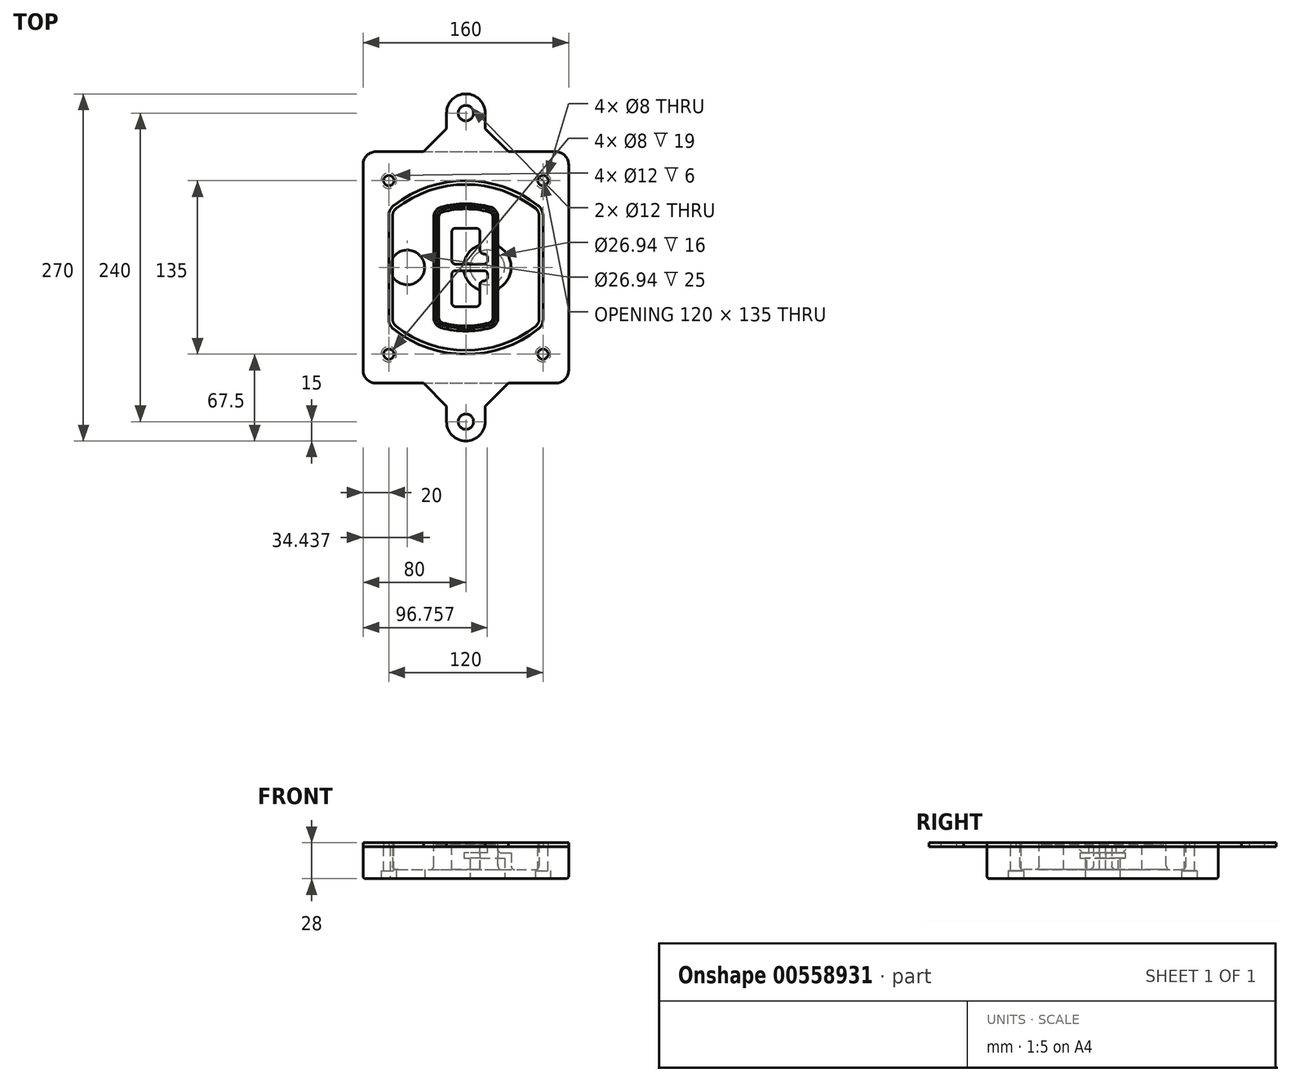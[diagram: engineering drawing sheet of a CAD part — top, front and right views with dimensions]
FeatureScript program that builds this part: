
annotation { "Feature Type Name" : "Feature", "Feature Type Description" : "" }
export const myFeature = defineFeature(function(context is Context, id is Id, definition is map)
    precondition{}
    {
        {
            var Q0;
            Q0=qCreatedBy(makeId("Top.planeOp"),FACE);
            var sketch = newSketch(context, id + "F0", { "sketchPlane" : qUnion([Q0])});
            skPoint(sketch, "E0.rect.middle", {"position": v(0, 0) * mm});
            skLineSegment(sketch, "E1.bottom", {"start": v(-70, -90) * mm, "end": v(70, -90) * mm});
            skLineSegment(sketch, "E1.top", {"start": v(-70, 90) * mm, "end": v(70, 90) * mm});
            skLineSegment(sketch, "E1.left", {"start": v(-80, -80) * mm, "end": v(-80, 80) * mm});
            skLineSegment(sketch, "E1.right", {"start": v(80, -80) * mm, "end": v(80, 80) * mm});
            skLineSegment(sketch, "E2", {"start": v(-80, 90) * mm, "end": v(80, -90) * mm, "construction": true});
            skLineSegment(sketch, "E3", {"start": v(80, 90) * mm, "end": v(-80, -90) * mm, "construction": true});
            skCircle(sketch, "E4", {"center": v(-60, 67.5) * mm, "radius": 4 * mm});
            skCircle(sketch, "E5", {"center": v(60, 67.5) * mm, "radius": 4 * mm});
            skCircle(sketch, "E6", {"center": v(60, -67.5) * mm, "radius": 4 * mm});
            skCircle(sketch, "E7", {"center": v(-60, -67.5) * mm, "radius": 4 * mm});
            skLineSegment(sketch, "E8", {"start": v(-60, 67.5) * mm, "end": v(60, 67.5) * mm, "construction": true});
            skLineSegment(sketch, "E9", {"start": v(60, 67.5) * mm, "end": v(60, -67.5) * mm, "construction": true});
            skLineSegment(sketch, "E10", {"start": v(60, -67.5) * mm, "end": v(-60, -67.5) * mm, "construction": true});
            skLineSegment(sketch, "E11", {"start": v(-60, -67.5) * mm, "end": v(-60, 67.5) * mm, "construction": true});
            skLineSegment(sketch, "E12", {"start": v(-60, 40.3) * mm, "end": v(-60, -40.3) * mm});
            skLineSegment(sketch, "E13", {"start": v(60, 40.3) * mm, "end": v(60, -40.3) * mm});
            skArc(sketch, "E14", {"start": v(56.15, 48.18) * mm, "mid": v(0, 67.5) * mm, "end": v(-56.15, 48.18) * mm});
            skArc(sketch, "E15", {"start": v(-56.15, -48.18) * mm, "mid": v(0, -67.5) * mm, "end": v(56.15, -48.18) * mm});
            skLineSegment(sketch, "E16", {"start": v(-60, 0) * mm, "end": v(60, 0) * mm, "construction": true});
            skPoint(sketch, "E17.visualSharp", {"position": v(-60, -45) * mm});
            skArc(sketch, "E17.filletArc", {"start": v(-60, -40.3) * mm, "mid": v(-58.99, -44.68) * mm, "end": v(-56.15, -48.18) * mm});
            skPoint(sketch, "E18.visualSharp", {"position": v(-60, 45) * mm});
            skArc(sketch, "E18.filletArc", {"start": v(-56.15, 48.18) * mm, "mid": v(-58.99, 44.68) * mm, "end": v(-60, 40.3) * mm});
            skPoint(sketch, "E19.visualSharp", {"position": v(60, 45) * mm});
            skArc(sketch, "E19.filletArc", {"start": v(60, 40.3) * mm, "mid": v(58.99, 44.68) * mm, "end": v(56.15, 48.18) * mm});
            skPoint(sketch, "E20.visualSharp", {"position": v(60, -45) * mm});
            skArc(sketch, "E20.filletArc", {"start": v(56.15, -48.18) * mm, "mid": v(58.99, -44.68) * mm, "end": v(60, -40.3) * mm});
            skPoint(sketch, "E21.visualSharp", {"position": v(-80, 90) * mm});
            skArc(sketch, "E21.filletArc", {"start": v(-70, 90) * mm, "mid": v(-77.07, 87.07) * mm, "end": v(-80, 80) * mm});
            skPoint(sketch, "E22.visualSharp", {"position": v(80, 90) * mm});
            skArc(sketch, "E22.filletArc", {"start": v(80, 80) * mm, "mid": v(77.07, 87.07) * mm, "end": v(70, 90) * mm});
            skPoint(sketch, "E23.visualSharp", {"position": v(80, -90) * mm});
            skArc(sketch, "E23.filletArc", {"start": v(70, -90) * mm, "mid": v(77.07, -87.07) * mm, "end": v(80, -80) * mm});
            skPoint(sketch, "E24.visualSharp", {"position": v(-80, -90) * mm});
            skArc(sketch, "E24.filletArc", {"start": v(-80, -80) * mm, "mid": v(-77.07, -87.07) * mm, "end": v(-70, -90) * mm});
            skArc(sketch, "E25.0", {"start": v(57, 40.3) * mm, "mid": v(56.3, 43.36) * mm, "end": v(54.3, 45.81) * mm});
            skLineSegment(sketch, "E25.1", {"start": v(57, 40.3) * mm, "end": v(57, -40.3) * mm});
            skArc(sketch, "E25.2", {"start": v(54.3, -45.81) * mm, "mid": v(56.3, -43.36) * mm, "end": v(57, -40.3) * mm});
            skArc(sketch, "E25.3", {"start": v(-54.3, -45.81) * mm, "mid": v(0, -64.5) * mm, "end": v(54.3, -45.81) * mm});
            skArc(sketch, "E25.4", {"start": v(-57, -40.3) * mm, "mid": v(-56.3, -43.36) * mm, "end": v(-54.3, -45.81) * mm});
            skArc(sketch, "E25.5", {"start": v(54.3, 45.81) * mm, "mid": v(0, 64.5) * mm, "end": v(-54.3, 45.81) * mm});
            skLineSegment(sketch, "E25.6", {"start": v(-57, 40.3) * mm, "end": v(-57, -40.3) * mm});
            skArc(sketch, "E25.7", {"start": v(-54.3, 45.81) * mm, "mid": v(-56.3, 43.36) * mm, "end": v(-57, 40.3) * mm});
            skArc(sketch, "E26.0", {"start": v(-58.62, 51.33) * mm, "mid": v(-62.58, 46.43) * mm, "end": v(-64, 40.3) * mm});
            skArc(sketch, "E26.1", {"start": v(58.62, 51.33) * mm, "mid": v(0, 71.5) * mm, "end": v(-58.62, 51.33) * mm});
            skArc(sketch, "E26.2", {"start": v(64, 40.3) * mm, "mid": v(62.58, 46.43) * mm, "end": v(58.62, 51.33) * mm});
            skLineSegment(sketch, "E26.3", {"start": v(64, 40.3) * mm, "end": v(64, -40.3) * mm});
            skArc(sketch, "E26.4", {"start": v(58.62, -51.33) * mm, "mid": v(62.58, -46.43) * mm, "end": v(64, -40.3) * mm});
            skLineSegment(sketch, "E26.5", {"start": v(-64, 40.3) * mm, "end": v(-64, -40.3) * mm});
            skArc(sketch, "E26.6", {"start": v(-58.62, -51.33) * mm, "mid": v(0, -71.5) * mm, "end": v(58.62, -51.33) * mm});
            skArc(sketch, "E26.7", {"start": v(-64, -40.3) * mm, "mid": v(-62.58, -46.43) * mm, "end": v(-58.62, -51.33) * mm});
            skSolve(sketch);
        }
        {
            var Q0;
            Q0=makeQuery(id+"F0.imprint","IMPRINT",FACE,{"disambiguationData":[TD([[makeQuery(id+"F0.imprint","IMPRINT",EDGE,{"derivedFrom":sQuery(id+"F0.wireOp",EDGE,"E1.bottom")}),1.0]])]});
            var Q1;
            Q1=makeQuery(id+"F0.imprint","IMPRINT",FACE,{"disambiguationData":[TD([[makeQuery(id+"F0.imprint","IMPRINT",EDGE,{"derivedFrom":sQuery(id+"F0.wireOp",EDGE,"E12")}),1.0]])]});
            var Q2;
            Q2=makeQuery(id+"F0.imprint","IMPRINT",FACE,{"disambiguationData":[TD([[makeQuery(id+"F0.imprint","IMPRINT",EDGE,{"derivedFrom":sQuery(id+"F0.wireOp",EDGE,"E25.0")}),1.0]])]});
            var Q3;
            Q3=makeQuery(id+"F0.imprint","IMPRINT",FACE,{"disambiguationData":[TD([[makeQuery(id+"F0.imprint","IMPRINT",EDGE,{"derivedFrom":sQuery(id+"F0.wireOp",EDGE,"E12")}),-1.0]])]});
            extrude(context, id + "F1", {"entities" : qUnion([Q0, Q1, Q2, Q3]), "oppositeDirection" : true, "depth" : 25 * mm});
        }
        {
            var Q0;
            Q0=makeQuery(id+"F0.imprint","IMPRINT",FACE,{"disambiguationData":[TD([[makeQuery(id+"F0.imprint","IMPRINT",EDGE,{"derivedFrom":sQuery(id+"F0.wireOp",EDGE,"E12")}),1.0]])]});
            extrude(context, id + "F2", {"entities" : qUnion([Q0]), "operationType" : NewBodyOperationType.ADD, "depth" : 3 * mm});
        }
        {
            var Q0;
            Q0=makeQuery(id+"F0.imprint","IMPRINT",FACE,{"disambiguationData":[TD([[makeQuery(id+"F0.imprint","IMPRINT",EDGE,{"derivedFrom":sQuery(id+"F0.wireOp",EDGE,"E25.0")}),1.0]])]});
            extrude(context, id + "F3", {"entities" : qUnion([Q0]), "operationType" : NewBodyOperationType.REMOVE, "oppositeDirection" : true, "depth" : 18 * mm});
        }
        {
            var Q0;
            Q0=makeQuery(id+"F2.opExtrude","CAP_FACE",FACE,{"disambiguationData":[OSD([sQuery(id+"F0.wireOp",EDGE,"E12"),sQuery(id+"F0.wireOp",EDGE,"E13"),sQuery(id+"F0.wireOp",EDGE,"E14"),sQuery(id+"F0.wireOp",EDGE,"E15"),sQuery(id+"F0.wireOp",EDGE,"E17.filletArc"),sQuery(id+"F0.wireOp",EDGE,"E18.filletArc"),sQuery(id+"F0.wireOp",EDGE,"E19.filletArc"),sQuery(id+"F0.wireOp",EDGE,"E20.filletArc"),sQuery(id+"F0.wireOp",EDGE,"E25.0"),sQuery(id+"F0.wireOp",EDGE,"E25.1"),sQuery(id+"F0.wireOp",EDGE,"E25.2"),sQuery(id+"F0.wireOp",EDGE,"E25.3"),sQuery(id+"F0.wireOp",EDGE,"E25.4"),sQuery(id+"F0.wireOp",EDGE,"E25.5"),sQuery(id+"F0.wireOp",EDGE,"E25.6"),sQuery(id+"F0.wireOp",EDGE,"E25.7")])],"isStart":false});
            var sketch = newSketch(context, id + "F4", { "sketchPlane" : qUnion([Q0])});
            skArc(sketch, "E27.0", {"start": v(-19.08, -46.97) * mm, "mid": v(0, -49.5) * mm, "end": v(19.08, -46.97) * mm});
            skArc(sketch, "E28.0", {"start": v(19.08, 46.97) * mm, "mid": v(0, 49.5) * mm, "end": v(-19.08, 46.97) * mm});
            skLineSegment(sketch, "E29", {"start": v(-25, 39.25) * mm, "end": v(-25, -39.25) * mm});
            skLineSegment(sketch, "E30", {"start": v(25, 39.25) * mm, "end": v(25, -39.25) * mm});
            skLineSegment(sketch, "E31", {"start": v(-25, 45.1) * mm, "end": v(25, 45.1) * mm, "construction": true});
            skLineSegment(sketch, "E32", {"start": v(-25, -45.1) * mm, "end": v(25, -45.1) * mm, "construction": true});
            skPoint(sketch, "E33.visualSharp", {"position": v(-25, 45.1) * mm});
            skArc(sketch, "E33.filletArc", {"start": v(-19.08, 46.97) * mm, "mid": v(-23.35, 44.11) * mm, "end": v(-25, 39.25) * mm});
            skPoint(sketch, "E34.visualSharp", {"position": v(25, 45.1) * mm});
            skArc(sketch, "E34.filletArc", {"start": v(25, 39.25) * mm, "mid": v(23.35, 44.11) * mm, "end": v(19.08, 46.97) * mm});
            skPoint(sketch, "E35.visualSharp", {"position": v(25, -45.1) * mm});
            skArc(sketch, "E35.filletArc", {"start": v(19.08, -46.97) * mm, "mid": v(23.35, -44.11) * mm, "end": v(25, -39.25) * mm});
            skPoint(sketch, "E36.visualSharp", {"position": v(-25, -45.1) * mm});
            skArc(sketch, "E36.filletArc", {"start": v(-25, -39.25) * mm, "mid": v(-23.35, -44.11) * mm, "end": v(-19.08, -46.97) * mm});
            skArc(sketch, "E37.0", {"start": v(54.3, 45.81) * mm, "mid": v(0, 64.5) * mm, "end": v(-54.3, 45.81) * mm});
            skArc(sketch, "E37.1", {"start": v(-54.3, 45.81) * mm, "mid": v(-56.3, 43.36) * mm, "end": v(-57, 40.3) * mm});
            skLineSegment(sketch, "E37.2", {"start": v(-57, 40.3) * mm, "end": v(-57, -40.3) * mm});
            skArc(sketch, "E37.3", {"start": v(-57, -40.3) * mm, "mid": v(-56.3, -43.36) * mm, "end": v(-54.3, -45.81) * mm});
            skArc(sketch, "E37.4", {"start": v(-54.3, -45.81) * mm, "mid": v(0, -64.5) * mm, "end": v(54.3, -45.81) * mm});
            skArc(sketch, "E37.5", {"start": v(54.3, -45.81) * mm, "mid": v(56.3, -43.36) * mm, "end": v(57, -40.3) * mm});
            skLineSegment(sketch, "E37.6", {"start": v(57, 40.3) * mm, "end": v(57, -40.3) * mm});
            skArc(sketch, "E37.7", {"start": v(57, 40.3) * mm, "mid": v(56.3, 43.36) * mm, "end": v(54.3, 45.81) * mm});
            skLineSegment(sketch, "E38.0", {"start": v(23, 39.25) * mm, "end": v(23, -39.25) * mm});
            skArc(sketch, "E38.1", {"start": v(18.56, -45.04) * mm, "mid": v(21.76, -42.9) * mm, "end": v(23, -39.25) * mm});
            skArc(sketch, "E38.2", {"start": v(-18.56, -45.04) * mm, "mid": v(0, -47.5) * mm, "end": v(18.56, -45.04) * mm});
            skArc(sketch, "E38.3", {"start": v(-23, -39.25) * mm, "mid": v(-21.76, -42.9) * mm, "end": v(-18.56, -45.04) * mm});
            skLineSegment(sketch, "E38.4", {"start": v(-23, 39.25) * mm, "end": v(-23, -39.25) * mm});
            skArc(sketch, "E38.5", {"start": v(23, 39.25) * mm, "mid": v(21.76, 42.9) * mm, "end": v(18.56, 45.04) * mm});
            skArc(sketch, "E38.6", {"start": v(-18.56, 45.04) * mm, "mid": v(-21.76, 42.9) * mm, "end": v(-23, 39.25) * mm});
            skArc(sketch, "E38.7", {"start": v(18.56, 45.04) * mm, "mid": v(0, 47.5) * mm, "end": v(-18.56, 45.04) * mm});
            skArc(sketch, "E39.0", {"start": v(21, 39.25) * mm, "mid": v(20.18, 41.68) * mm, "end": v(18.04, 43.1) * mm});
            skLineSegment(sketch, "E39.1", {"start": v(21, 39.25) * mm, "end": v(21, -39.25) * mm});
            skArc(sketch, "E39.2", {"start": v(18.04, -43.1) * mm, "mid": v(20.18, -41.68) * mm, "end": v(21, -39.25) * mm});
            skArc(sketch, "E39.3", {"start": v(-18.04, -43.1) * mm, "mid": v(0, -45.5) * mm, "end": v(18.04, -43.1) * mm});
            skArc(sketch, "E39.4", {"start": v(-21, -39.25) * mm, "mid": v(-20.18, -41.68) * mm, "end": v(-18.04, -43.1) * mm});
            skArc(sketch, "E39.5", {"start": v(18.04, 43.1) * mm, "mid": v(0, 45.5) * mm, "end": v(-18.04, 43.1) * mm});
            skLineSegment(sketch, "E39.6", {"start": v(-21, 39.25) * mm, "end": v(-21, -39.25) * mm});
            skArc(sketch, "E39.7", {"start": v(-18.04, 43.1) * mm, "mid": v(-20.18, 41.68) * mm, "end": v(-21, 39.25) * mm});
            skLineSegment(sketch, "E40", {"start": v(-25, 0) * mm, "end": v(25, 0) * mm, "construction": true});
            skLineSegment(sketch, "E41", {"start": v(-11, 5.5) * mm, "end": v(-11, 27.5) * mm});
            skLineSegment(sketch, "E42", {"start": v(-8, 30.5) * mm, "end": v(8, 30.5) * mm});
            skLineSegment(sketch, "E43", {"start": v(11, 27.5) * mm, "end": v(11, 13.5) * mm});
            skLineSegment(sketch, "E44", {"start": v(14, 10.5) * mm, "end": v(14, 10.5) * mm});
            skLineSegment(sketch, "E45", {"start": v(17, 7.5) * mm, "end": v(17, 5.5) * mm});
            skLineSegment(sketch, "E46", {"start": v(14, 2.5) * mm, "end": v(-8, 2.5) * mm});
            skPoint(sketch, "E47.visualSharp", {"position": v(-11, 30.5) * mm});
            skArc(sketch, "E47.filletArc", {"start": v(-8, 30.5) * mm, "mid": v(-10.12, 29.62) * mm, "end": v(-11, 27.5) * mm});
            skPoint(sketch, "E48.visualSharp", {"position": v(11, 30.5) * mm});
            skArc(sketch, "E48.filletArc", {"start": v(11, 27.5) * mm, "mid": v(10.12, 29.62) * mm, "end": v(8, 30.5) * mm});
            skPoint(sketch, "E49.visualSharp", {"position": v(11, 10.5) * mm});
            skArc(sketch, "E49.filletArc", {"start": v(11, 13.5) * mm, "mid": v(11.88, 11.38) * mm, "end": v(14, 10.5) * mm});
            skPoint(sketch, "E50.visualSharp", {"position": v(17, 10.5) * mm});
            skArc(sketch, "E50.filletArc", {"start": v(17, 7.5) * mm, "mid": v(16.12, 9.62) * mm, "end": v(14, 10.5) * mm});
            skPoint(sketch, "E51.visualSharp", {"position": v(17, 2.5) * mm});
            skArc(sketch, "E51.filletArc", {"start": v(14, 2.5) * mm, "mid": v(16.12, 3.38) * mm, "end": v(17, 5.5) * mm});
            skPoint(sketch, "E52.visualSharp", {"position": v(-11, 2.5) * mm});
            skArc(sketch, "E52.filletArc", {"start": v(-11, 5.5) * mm, "mid": v(-10.12, 3.38) * mm, "end": v(-8, 2.5) * mm});
            skLineSegment(sketch, "E53.0.MirrorCS", {"start": v(14, -2.5) * mm, "end": v(-8, -2.5) * mm});
            skArc(sketch, "E54.0.MirrorCS", {"start": v(-11, -5.5) * mm, "mid": v(-10.12, -3.38) * mm, "end": v(-8, -2.5) * mm});
            skLineSegment(sketch, "E55.0.MirrorCS", {"start": v(-11, -5.5) * mm, "end": v(-11, -27.5) * mm});
            skArc(sketch, "E56.0.MirrorCS", {"start": v(-8, -30.5) * mm, "mid": v(-10.12, -29.62) * mm, "end": v(-11, -27.5) * mm});
            skLineSegment(sketch, "E57.0.MirrorCS", {"start": v(-8, -30.5) * mm, "end": v(8, -30.5) * mm});
            skArc(sketch, "E58.0.MirrorCS", {"start": v(11, -27.5) * mm, "mid": v(10.12, -29.62) * mm, "end": v(8, -30.5) * mm});
            skLineSegment(sketch, "E59.0.MirrorCS", {"start": v(11, -27.5) * mm, "end": v(11, -13.5) * mm});
            skArc(sketch, "E60.0.MirrorCS", {"start": v(11, -13.5) * mm, "mid": v(11.88, -11.38) * mm, "end": v(14, -10.5) * mm});
            skArc(sketch, "E61.0.MirrorCS", {"start": v(17, -7.5) * mm, "mid": v(16.12, -9.62) * mm, "end": v(14, -10.5) * mm});
            skLineSegment(sketch, "E62.0.MirrorCS", {"start": v(17, -7.5) * mm, "end": v(17, -5.5) * mm});
            skArc(sketch, "E63.0.MirrorCS", {"start": v(14, -2.5) * mm, "mid": v(16.12, -3.38) * mm, "end": v(17, -5.5) * mm});
            skSolve(sketch);
        }
        {
            var Q0;
            Q0=makeQuery(id+"F4.imprint","IMPRINT",FACE,{"disambiguationData":[TD([[makeQuery(id+"F4.imprint","IMPRINT",EDGE,{"derivedFrom":sQuery(id+"F4.wireOp",EDGE,"E27.0")}),1.0]])]});
            var Q1;
            Q1=makeQuery(id+"F4.imprint","IMPRINT",FACE,{"disambiguationData":[TD([[makeQuery(id+"F4.imprint","IMPRINT",EDGE,{"derivedFrom":sQuery(id+"F4.wireOp",EDGE,"E38.0")}),-1.0]])]});
            var Q2;
            Q2=makeQuery(id+"F4.imprint","IMPRINT",FACE,{"disambiguationData":[TD([[makeQuery(id+"F4.imprint","IMPRINT",EDGE,{"derivedFrom":sQuery(id+"F4.wireOp",EDGE,"E39.0")}),1.0]])]});
            extrude(context, id + "F5", {"entities" : qUnion([Q0, Q1, Q2]), "operationType" : NewBodyOperationType.ADD, "endBound" : BoundingType.UP_TO_NEXT, "oppositeDirection" : true, "depth" : 25 * mm});
        }
        {
            var Q0;
            Q0=makeQuery(id+"F4.imprint","IMPRINT",FACE,{"disambiguationData":[TD([[makeQuery(id+"F4.imprint","IMPRINT",EDGE,{"derivedFrom":sQuery(id+"F4.wireOp",EDGE,"E38.0")}),-1.0]])]});
            extrude(context, id + "F6", {"entities" : qUnion([Q0]), "operationType" : NewBodyOperationType.REMOVE, "oppositeDirection" : true, "depth" : 2 * mm});
        }
        {
            var Q0;
            Q0=makeQuery(id+"F1.opExtrude","CAP_FACE",FACE,{"disambiguationData":[OSD([sQuery(id+"F0.wireOp",EDGE,"E1.bottom"),sQuery(id+"F0.wireOp",EDGE,"E1.top"),sQuery(id+"F0.wireOp",EDGE,"E1.left"),sQuery(id+"F0.wireOp",EDGE,"E1.right"),sQuery(id+"F0.wireOp",EDGE,"E4"),sQuery(id+"F0.wireOp",EDGE,"E5"),sQuery(id+"F0.wireOp",EDGE,"E6"),sQuery(id+"F0.wireOp",EDGE,"E7"),sQuery(id+"F0.wireOp",EDGE,"E21.filletArc"),sQuery(id+"F0.wireOp",EDGE,"E22.filletArc"),sQuery(id+"F0.wireOp",EDGE,"E23.filletArc"),sQuery(id+"F0.wireOp",EDGE,"E24.filletArc")])],"isStart":false});
            var sketch = newSketch(context, id + "F7", { "sketchPlane" : qUnion([Q0])});
            skCircle(sketch, "E64", {"center": v(16.76, 0) * mm, "radius": 13.47 * mm});
            skCircle(sketch, "E65", {"center": v(-45.56, 0) * mm, "radius": 13.47 * mm});
            skLineSegment(sketch, "E66", {"start": v(80, 0) * mm, "end": v(-80, 0) * mm});
            skCircle(sketch, "E67", {"center": v(16.76, 0) * mm, "radius": 18.47 * mm});
            skCircle(sketch, "E68", {"center": v(60, -67.5) * mm, "radius": 6 * mm});
            skCircle(sketch, "E69", {"center": v(-60, -67.5) * mm, "radius": 6 * mm});
            skCircle(sketch, "E70", {"center": v(-60, 67.5) * mm, "radius": 6 * mm});
            skCircle(sketch, "E71", {"center": v(60, 67.5) * mm, "radius": 6 * mm});
            skSolve(sketch);
        }
        {
            var Q0;
            {var subQ1=sQuery(id+"F7.wireOp",EDGE,"E66");var subQ4=sQuery(id+"F7.wireOp",EDGE,"E64");var subQ6=makeQuery(id+"F7.imprint","INTERSECT",VERTEX,{"disambiguationData":[OD(0.0)],"derivedFrom":[subQ4,subQ1]});Q0=makeQuery(id+"F7.imprint","IMPRINT",FACE,{"disambiguationData":[TD([[makeQuery(id+"F7.imprint","IMPRINT",EDGE,{"disambiguationData":[TD([[subQ6,-1.0]])],"derivedFrom":subQ4}),-1.0]])]});}
            var Q1;
            {var subQ0=sQuery(id+"F7.wireOp",EDGE,"E66");var subQ1=sQuery(id+"F7.wireOp",EDGE,"E64");var subQ3=makeQuery(id+"F7.imprint","INTERSECT",VERTEX,{"disambiguationData":[OD(0.0)],"derivedFrom":[subQ1,subQ0]});Q1=makeQuery(id+"F7.imprint","IMPRINT",FACE,{"disambiguationData":[TD([[makeQuery(id+"F7.imprint","IMPRINT",EDGE,{"disambiguationData":[TD([[subQ3,-1.0]])],"derivedFrom":subQ1}),1.0]])]});}
            var Q2;
            {var subQ0=sQuery(id+"F7.wireOp",EDGE,"E66");var subQ1=sQuery(id+"F7.wireOp",EDGE,"E64");var subQ3=makeQuery(id+"F7.imprint","INTERSECT",VERTEX,{"disambiguationData":[OD(0.0)],"derivedFrom":[subQ1,subQ0]});Q2=makeQuery(id+"F7.imprint","IMPRINT",FACE,{"disambiguationData":[TD([[makeQuery(id+"F7.imprint","IMPRINT",EDGE,{"disambiguationData":[TD([[subQ3,1.0]])],"derivedFrom":subQ1}),1.0]])]});}
            var Q3;
            {var subQ1=sQuery(id+"F7.wireOp",EDGE,"E66");var subQ4=sQuery(id+"F7.wireOp",EDGE,"E64");var subQ6=makeQuery(id+"F7.imprint","INTERSECT",VERTEX,{"disambiguationData":[OD(0.0)],"derivedFrom":[subQ4,subQ1]});Q3=makeQuery(id+"F7.imprint","IMPRINT",FACE,{"disambiguationData":[TD([[makeQuery(id+"F7.imprint","IMPRINT",EDGE,{"disambiguationData":[TD([[subQ6,1.0]])],"derivedFrom":subQ4}),-1.0]])]});}
            extrude(context, id + "F8", {"entities" : qUnion([Q0, Q1, Q2, Q3]), "operationType" : NewBodyOperationType.ADD, "oppositeDirection" : true, "depth" : 20 * mm});
        }
        {
            var Q0;
            {var subQ0=sQuery(id+"F7.wireOp",EDGE,"E66");var subQ1=sQuery(id+"F7.wireOp",EDGE,"E64");var subQ3=makeQuery(id+"F7.imprint","INTERSECT",VERTEX,{"disambiguationData":[OD(0.0)],"derivedFrom":[subQ1,subQ0]});Q0=makeQuery(id+"F7.imprint","IMPRINT",FACE,{"disambiguationData":[TD([[makeQuery(id+"F7.imprint","IMPRINT",EDGE,{"disambiguationData":[TD([[subQ3,-1.0]])],"derivedFrom":subQ1}),1.0]])]});}
            var Q1;
            {var subQ0=sQuery(id+"F7.wireOp",EDGE,"E66");var subQ1=sQuery(id+"F7.wireOp",EDGE,"E64");var subQ3=makeQuery(id+"F7.imprint","INTERSECT",VERTEX,{"disambiguationData":[OD(0.0)],"derivedFrom":[subQ1,subQ0]});Q1=makeQuery(id+"F7.imprint","IMPRINT",FACE,{"disambiguationData":[TD([[makeQuery(id+"F7.imprint","IMPRINT",EDGE,{"disambiguationData":[TD([[subQ3,1.0]])],"derivedFrom":subQ1}),1.0]])]});}
            extrude(context, id + "F9", {"entities" : qUnion([Q0, Q1]), "operationType" : NewBodyOperationType.REMOVE, "oppositeDirection" : true, "depth" : 16 * mm});
        }
        {
            var Q0;
            {var subQ0=sQuery(id+"F7.wireOp",EDGE,"E66");var subQ1=sQuery(id+"F7.wireOp",EDGE,"E65");var subQ3=makeQuery(id+"F7.imprint","INTERSECT",VERTEX,{"disambiguationData":[OD(0.0)],"derivedFrom":[subQ1,subQ0]});Q0=makeQuery(id+"F7.imprint","IMPRINT",FACE,{"disambiguationData":[TD([[makeQuery(id+"F7.imprint","IMPRINT",EDGE,{"disambiguationData":[TD([[subQ3,-1.0]])],"derivedFrom":subQ1}),1.0]])]});}
            var Q1;
            {var subQ0=sQuery(id+"F7.wireOp",EDGE,"E66");var subQ1=sQuery(id+"F7.wireOp",EDGE,"E65");var subQ3=makeQuery(id+"F7.imprint","INTERSECT",VERTEX,{"disambiguationData":[OD(0.0)],"derivedFrom":[subQ1,subQ0]});Q1=makeQuery(id+"F7.imprint","IMPRINT",FACE,{"disambiguationData":[TD([[makeQuery(id+"F7.imprint","IMPRINT",EDGE,{"disambiguationData":[TD([[subQ3,1.0]])],"derivedFrom":subQ1}),1.0]])]});}
            extrude(context, id + "F10", {"entities" : qUnion([Q0, Q1]), "operationType" : NewBodyOperationType.REMOVE, "oppositeDirection" : true, "depth" : 25 * mm});
        }
        {
            var Q0;
            Q0=makeQuery(id+"F7.imprint","IMPRINT",FACE,{"disambiguationData":[TD([[makeQuery(id+"F7.imprint","IMPRINT",EDGE,{"derivedFrom":sQuery(id+"F7.wireOp",EDGE,"E68")}),1.0]])]});
            var Q1;
            Q1=makeQuery(id+"F7.imprint","IMPRINT",FACE,{"disambiguationData":[TD([[makeQuery(id+"F7.imprint","IMPRINT",EDGE,{"derivedFrom":makeQuery(id+"F1.opExtrude","CAP_EDGE",EDGE,{"disambiguationData":[OSD([sQuery(id+"F0.wireOp",EDGE,"E5")])],"isStart":false})}),-1.0]])]});
            var Q2;
            Q2=makeQuery(id+"F7.imprint","IMPRINT",FACE,{"disambiguationData":[TD([[makeQuery(id+"F7.imprint","IMPRINT",EDGE,{"derivedFrom":sQuery(id+"F7.wireOp",EDGE,"E69")}),1.0]])]});
            var Q3;
            Q3=makeQuery(id+"F7.imprint","IMPRINT",FACE,{"disambiguationData":[TD([[makeQuery(id+"F7.imprint","IMPRINT",EDGE,{"derivedFrom":makeQuery(id+"F1.opExtrude","CAP_EDGE",EDGE,{"disambiguationData":[OSD([sQuery(id+"F0.wireOp",EDGE,"E4")])],"isStart":false})}),-1.0]])]});
            var Q4;
            Q4=makeQuery(id+"F7.imprint","IMPRINT",FACE,{"disambiguationData":[TD([[makeQuery(id+"F7.imprint","IMPRINT",EDGE,{"derivedFrom":sQuery(id+"F7.wireOp",EDGE,"E70")}),1.0]])]});
            var Q5;
            Q5=makeQuery(id+"F7.imprint","IMPRINT",FACE,{"disambiguationData":[TD([[makeQuery(id+"F7.imprint","IMPRINT",EDGE,{"derivedFrom":makeQuery(id+"F1.opExtrude","CAP_EDGE",EDGE,{"disambiguationData":[OSD([sQuery(id+"F0.wireOp",EDGE,"E7")])],"isStart":false})}),-1.0]])]});
            var Q6;
            Q6=makeQuery(id+"F7.imprint","IMPRINT",FACE,{"disambiguationData":[TD([[makeQuery(id+"F7.imprint","IMPRINT",EDGE,{"derivedFrom":sQuery(id+"F7.wireOp",EDGE,"E71")}),1.0]])]});
            var Q7;
            Q7=makeQuery(id+"F7.imprint","IMPRINT",FACE,{"disambiguationData":[TD([[makeQuery(id+"F7.imprint","IMPRINT",EDGE,{"derivedFrom":makeQuery(id+"F1.opExtrude","CAP_EDGE",EDGE,{"disambiguationData":[OSD([sQuery(id+"F0.wireOp",EDGE,"E6")])],"isStart":false})}),-1.0]])]});
            extrude(context, id + "F11", {"entities" : qUnion([Q0, Q1, Q2, Q3, Q4, Q5, Q6, Q7]), "operationType" : NewBodyOperationType.REMOVE, "oppositeDirection" : true, "depth" : 6 * mm});
        }
        {
            var Q0;
            Q0=makeQuery(id+"F9.boolean.opBoolean","COPY",FACE,{"derivedFrom":makeQuery(id+"F9.opExtrude","CAP_FACE",FACE,{"disambiguationData":[OSD([sQuery(id+"F7.wireOp",EDGE,"E64")])],"isStart":false})});
            var sketch = newSketch(context, id + "F12", { "sketchPlane" : qUnion([Q0])});
            skArc(sketch, "E72.0", {"start": v(11, 17.55) * mm, "mid": v(2.57, 11.82) * mm, "end": v(-1.54, 2.5) * mm});
            skArc(sketch, "E72.1", {"start": v(-1.54, -2.5) * mm, "mid": v(2.57, -11.82) * mm, "end": v(11, -17.55) * mm});
            skLineSegment(sketch, "E73", {"start": v(-1.54, -2.5) * mm, "end": v(14, -2.5) * mm});
            skLineSegment(sketch, "E74.0", {"start": v(14, 2.5) * mm, "end": v(-1.54, 2.5) * mm});
            skArc(sketch, "E74.1", {"start": v(14, 2.5) * mm, "mid": v(16.12, 3.38) * mm, "end": v(17, 5.5) * mm});
            skLineSegment(sketch, "E74.2", {"start": v(17, 7.5) * mm, "end": v(17, 5.5) * mm});
            skArc(sketch, "E74.3", {"start": v(17, 7.5) * mm, "mid": v(16.12, 9.62) * mm, "end": v(14, 10.5) * mm});
            skArc(sketch, "E74.4", {"start": v(11, 13.5) * mm, "mid": v(11.88, 11.38) * mm, "end": v(14, 10.5) * mm});
            skLineSegment(sketch, "E74.5", {"start": v(11, 17.55) * mm, "end": v(11, 13.5) * mm});
            skLineSegment(sketch, "E74.7", {"start": v(14, -2.5) * mm, "end": v(-1.54, -2.5) * mm});
            skArc(sketch, "E74.8", {"start": v(14, -2.5) * mm, "mid": v(16.12, -3.38) * mm, "end": v(17, -5.5) * mm});
            skLineSegment(sketch, "E74.9", {"start": v(17, -7.5) * mm, "end": v(17, -5.5) * mm});
            skArc(sketch, "E74.10", {"start": v(17, -7.5) * mm, "mid": v(16.12, -9.62) * mm, "end": v(14, -10.5) * mm});
            skArc(sketch, "E74.11", {"start": v(11, -13.5) * mm, "mid": v(11.88, -11.38) * mm, "end": v(14, -10.5) * mm});
            skLineSegment(sketch, "E74.12", {"start": v(11, -17.55) * mm, "end": v(11, -13.5) * mm});
            skPoint(sketch, "E75.orphan", {"position": v(11, -27.5) * mm});
            skPoint(sketch, "E76.orphan", {"position": v(-8, -2.5) * mm});
            skPoint(sketch, "E77.orphan", {"position": v(-8, 2.5) * mm});
            skPoint(sketch, "E78.orphan", {"position": v(11, 27.5) * mm});
            skSolve(sketch);
        }
        {
            var Q0;
            {var subQ7=sQuery(id+"F12.wireOp",EDGE,"E72.0");var subQ14=sQuery(id+"F12.wireOp",EDGE,"E72.1");var subQ16=sQuery(id+"F12.wireOp",EDGE,"E74.1");var subQ18=sQuery(id+"F12.wireOp",EDGE,"E74.8");Q0=qUnion([makeQuery(id+"F12.imprint","IMPRINT",FACE,{"disambiguationData":[TD([[makeQuery(id+"F12.imprint","IMPRINT",EDGE,{"derivedFrom":subQ7}),1.0]])]}),makeQuery(id+"F12.imprint","IMPRINT",FACE,{"disambiguationData":[TD([[makeQuery(id+"F12.imprint","IMPRINT",EDGE,{"derivedFrom":subQ14}),1.0]])]}),makeQuery(id+"F12.imprint","IMPRINT",FACE,{"disambiguationData":[TD([[makeQuery(id+"F12.imprint","IMPRINT",EDGE,{"derivedFrom":subQ16}),1.0]])]}),makeQuery(id+"F12.imprint","IMPRINT",FACE,{"disambiguationData":[TD([[makeQuery(id+"F12.imprint","IMPRINT",EDGE,{"derivedFrom":subQ18}),-1.0]])]})]);}
            var Q1;
            Q1=makeQuery(id+"F5.boolean.opBoolean","SPLIT",FACE,{"disambiguationData":[TD([makeQuery(id+"F5.opExtrude","SWEPT_FACE",FACE,{"disambiguationData":[OSD([sQuery(id+"F4.wireOp",EDGE,"E41")])]})])],"derivedFrom":makeQuery(id+"F3.boolean.opBoolean","COPY",FACE,{"derivedFrom":makeQuery(id+"F3.opExtrude","CAP_FACE",FACE,{"disambiguationData":[OSD([sQuery(id+"F0.wireOp",EDGE,"E25.0"),sQuery(id+"F0.wireOp",EDGE,"E25.1"),sQuery(id+"F0.wireOp",EDGE,"E25.2"),sQuery(id+"F0.wireOp",EDGE,"E25.3"),sQuery(id+"F0.wireOp",EDGE,"E25.4"),sQuery(id+"F0.wireOp",EDGE,"E25.5"),sQuery(id+"F0.wireOp",EDGE,"E25.6"),sQuery(id+"F0.wireOp",EDGE,"E25.7")])],"isStart":false})})});
            extrude(context, id + "F13", {"entities" : qUnion([Q0]), "operationType" : NewBodyOperationType.REMOVE, "endBound" : BoundingType.UP_TO_SURFACE, "endBoundEntityFace" : qUnion([Q1]), "depth" : 25 * mm});
        }
        {
            var Q0;
            Q0=makeQuery(id+"F3.boolean.opBoolean","COPY",EDGE,{"derivedFrom":makeQuery(id+"F3.opExtrude","CAP_EDGE",EDGE,{"disambiguationData":[OSD([sQuery(id+"F0.wireOp",EDGE,"E25.6")])],"isStart":false})});
            var Q1;
            Q1=makeQuery(id+"F8.boolean.opBoolean","INTERSECT",EDGE,{"derivedFrom":[makeQuery(id+"F5.opExtrude","SWEPT_FACE",FACE,{"disambiguationData":[OSD([sQuery(id+"F4.wireOp",EDGE,"E30")])]}),makeQuery(id+"F8.opExtrude","CAP_FACE",FACE,{"disambiguationData":[OSD([sQuery(id+"F7.wireOp",EDGE,"E67")])],"isStart":false})]});
            var Q2;
            Q2=makeQuery(id+"F8.boolean.opBoolean","INTERSECT",EDGE,{"disambiguationData":[OD(1.0)],"derivedFrom":[makeQuery(id+"F5.opExtrude","SWEPT_FACE",FACE,{"disambiguationData":[OSD([sQuery(id+"F4.wireOp",EDGE,"E30")])]}),makeQuery(id+"F8.opExtrude","SWEPT_FACE",FACE,{"disambiguationData":[OSD([sQuery(id+"F7.wireOp",EDGE,"E67")])]})]});
            var Q3;
            {var subQ0=sQuery(id+"F4.wireOp",EDGE,"E30");Q3=makeQuery(id+"F8.boolean.opBoolean","SPLIT",EDGE,{"disambiguationData":[TD([makeQuery(id+"F5.opExtrude","SWEPT_FACE",FACE,{"disambiguationData":[OSD([sQuery(id+"F4.wireOp",EDGE,"E35.filletArc")])]})])],"derivedFrom":makeQuery(id+"F5.opExtrude","CAP_EDGE",EDGE,{"disambiguationData":[OSD([subQ0])],"isStart":false})});}
            var Q4;
            {var subQ0=sQuery(id+"F0.wireOp",EDGE,"E25.7");var subQ1=sQuery(id+"F0.wireOp",EDGE,"E25.1");var subQ2=sQuery(id+"F0.wireOp",EDGE,"E25.6");var subQ3=sQuery(id+"F0.wireOp",EDGE,"E25.5");var subQ4=sQuery(id+"F0.wireOp",EDGE,"E25.4");var subQ5=sQuery(id+"F0.wireOp",EDGE,"E25.0");var subQ6=sQuery(id+"F0.wireOp",EDGE,"E25.2");var subQ7=sQuery(id+"F0.wireOp",EDGE,"E25.3");Q4=makeQuery(id+"F8.boolean.opBoolean","INTERSECT",EDGE,{"derivedFrom":[makeQuery(id+"F5.boolean.opBoolean","SPLIT",FACE,{"disambiguationData":[TD([makeQuery(id+"F2.opExtrude","SWEPT_FACE",FACE,{"disambiguationData":[OSD([subQ5])]})])],"derivedFrom":makeQuery(id+"F3.boolean.opBoolean","COPY",FACE,{"derivedFrom":makeQuery(id+"F3.opExtrude","CAP_FACE",FACE,{"disambiguationData":[OSD([subQ5,subQ1,subQ6,subQ7,subQ4,subQ3,subQ2,subQ0])],"isStart":false})})}),makeQuery(id+"F8.opExtrude","SWEPT_FACE",FACE,{"disambiguationData":[OSD([sQuery(id+"F7.wireOp",EDGE,"E67")])]})]});}
            var Q5;
            Q5=makeQuery(id+"F8.boolean.opBoolean","INTERSECT",EDGE,{"disambiguationData":[OD(0.0)],"derivedFrom":[makeQuery(id+"F5.opExtrude","SWEPT_FACE",FACE,{"disambiguationData":[OSD([sQuery(id+"F4.wireOp",EDGE,"E30")])]}),makeQuery(id+"F8.opExtrude","SWEPT_FACE",FACE,{"disambiguationData":[OSD([sQuery(id+"F7.wireOp",EDGE,"E67")])]})]});
            fillet(context, id + "F14", {"entities" : qUnion([Q0, Q1, Q2, Q3, Q4, Q5]), "radius" : 3 * mm, "tangentPropagation" : true, "allowEdgeOverflow" : false});
        }
        {
            var Q0;
            Q0=makeQuery(id+"F1.opExtrude","CAP_EDGE",EDGE,{"disambiguationData":[OSD([sQuery(id+"F0.wireOp",EDGE,"E1.bottom")])],"isStart":false});
            fillet(context, id + "F15", {"entities" : qUnion([Q0]), "radius" : 2 * mm, "tangentPropagation" : true, "allowEdgeOverflow" : false});
        }
        {
            var Q0;
            {var subQ0=sQuery(id+"F0.wireOp",EDGE,"E21.filletArc");var subQ1=sQuery(id+"F0.wireOp",EDGE,"E7");var subQ2=sQuery(id+"F0.wireOp",EDGE,"E6");var subQ3=sQuery(id+"F0.wireOp",EDGE,"E5");var subQ4=sQuery(id+"F0.wireOp",EDGE,"E4");var subQ5=sQuery(id+"F0.wireOp",EDGE,"E22.filletArc");var subQ6=sQuery(id+"F0.wireOp",EDGE,"E1.bottom");var subQ7=sQuery(id+"F0.wireOp",EDGE,"E1.right");var subQ8=sQuery(id+"F0.wireOp",EDGE,"E1.top");var subQ9=sQuery(id+"F0.wireOp",EDGE,"E1.left");var subQ10=sQuery(id+"F0.wireOp",EDGE,"E23.filletArc");var subQ11=sQuery(id+"F0.wireOp",EDGE,"E24.filletArc");Q0=makeQuery(id+"F2.boolean.opBoolean","SPLIT",FACE,{"disambiguationData":[TD([makeQuery(id+"F1.opExtrude","SWEPT_FACE",FACE,{"disambiguationData":[OSD([subQ6])]})])],"derivedFrom":makeQuery(id+"F1.opExtrude","CAP_FACE",FACE,{"disambiguationData":[OSD([subQ6,subQ8,subQ9,subQ7,subQ4,subQ3,subQ2,subQ1,subQ0,subQ5,subQ10,subQ11])],"isStart":true})});}
            var sketch = newSketch(context, id + "F16", { "sketchPlane" : qUnion([Q0])});
            skArc(sketch, "E79.0", {"start": v(56.15, 48.18) * mm, "mid": v(0, 67.5) * mm, "end": v(-56.15, 48.18) * mm});
            skLineSegment(sketch, "E79.1", {"start": v(-60, 40.3) * mm, "end": v(-60, -40.3) * mm});
            skArc(sketch, "E79.2", {"start": v(-56.15, -48.18) * mm, "mid": v(0, -67.5) * mm, "end": v(56.15, -48.18) * mm});
            skLineSegment(sketch, "E79.3", {"start": v(60, 40.3) * mm, "end": v(60, -40.3) * mm});
            skLineSegment(sketch, "E79.4", {"start": v(-70, 90) * mm, "end": v(70, 90) * mm});
            skArc(sketch, "E79.5", {"start": v(80, 80) * mm, "mid": v(77.07, 87.07) * mm, "end": v(70, 90) * mm});
            skLineSegment(sketch, "E79.6", {"start": v(80, -80) * mm, "end": v(80, 80) * mm});
            skArc(sketch, "E79.7", {"start": v(70, -90) * mm, "mid": v(77.07, -87.07) * mm, "end": v(80, -80) * mm});
            skLineSegment(sketch, "E79.8", {"start": v(-70, -90) * mm, "end": v(70, -90) * mm});
            skArc(sketch, "E79.9", {"start": v(-80, -80) * mm, "mid": v(-77.07, -87.07) * mm, "end": v(-70, -90) * mm});
            skLineSegment(sketch, "E79.10", {"start": v(-80, -80) * mm, "end": v(-80, 80) * mm});
            skArc(sketch, "E79.11", {"start": v(-70, 90) * mm, "mid": v(-77.07, 87.07) * mm, "end": v(-80, 80) * mm});
            skArc(sketch, "E79.12", {"start": v(-56.15, 48.18) * mm, "mid": v(-58.99, 44.68) * mm, "end": v(-60, 40.3) * mm});
            skArc(sketch, "E79.13", {"start": v(-60, -40.3) * mm, "mid": v(-58.99, -44.68) * mm, "end": v(-56.15, -48.18) * mm});
            skArc(sketch, "E79.14", {"start": v(56.15, -48.18) * mm, "mid": v(58.99, -44.68) * mm, "end": v(60, -40.3) * mm});
            skArc(sketch, "E79.15", {"start": v(60, 40.3) * mm, "mid": v(58.99, 44.68) * mm, "end": v(56.15, 48.18) * mm});
            skLineSegment(sketch, "E80", {"start": v(0, 50.03) * mm, "end": v(0, 142.28) * mm, "construction": true});
            skLineSegment(sketch, "E81", {"start": v(-33, 90) * mm, "end": v(-15, 108) * mm});
            skLineSegment(sketch, "E82", {"start": v(-15, 108) * mm, "end": v(-15, 120) * mm});
            skLineSegment(sketch, "E83", {"start": v(33, 90) * mm, "end": v(15, 108) * mm});
            skLineSegment(sketch, "E84", {"start": v(15, 108) * mm, "end": v(15, 120) * mm});
            skArc(sketch, "E85", {"start": v(15, 120) * mm, "mid": v(0, 135) * mm, "end": v(-15, 120) * mm});
            skCircle(sketch, "E86", {"center": v(0, 120) * mm, "radius": 6 * mm});
            skLineSegment(sketch, "E87", {"start": v(94.87, 0) * mm, "end": v(-91.8, 0) * mm, "construction": true});
            skPoint(sketch, "E87.startSnap0", {"position": v(80, 0) * mm});
            skPoint(sketch, "E87.endSnap0", {"position": v(-80, 0) * mm});
            skLineSegment(sketch, "E88.MirrorCS", {"start": v(-33, -90) * mm, "end": v(-15, -108) * mm});
            skLineSegment(sketch, "E89.MirrorCS", {"start": v(-15, -108) * mm, "end": v(-15, -120) * mm});
            skArc(sketch, "E90.MirrorCS", {"start": v(15, -120) * mm, "mid": v(0, -135) * mm, "end": v(-15, -120) * mm});
            skCircle(sketch, "E91.MirrorC", {"center": v(0, -120) * mm, "radius": 6 * mm});
            skLineSegment(sketch, "E92.MirrorCS", {"start": v(15, -108) * mm, "end": v(15, -120) * mm});
            skLineSegment(sketch, "E93.MirrorCS", {"start": v(33, -90) * mm, "end": v(15, -108) * mm});
            skSolve(sketch);
        }
        {
            var Q0;
            {var subQ1=sQuery(id+"F16.wireOp",EDGE,"E81");Q0=makeQuery(id+"F16.imprint","IMPRINT",FACE,{"disambiguationData":[TD([[makeQuery(id+"F16.imprint","IMPRINT",EDGE,{"derivedFrom":subQ1}),-1.0]])]});}
            var Q1;
            {var subQ0=sQuery(id+"F16.wireOp",EDGE,"E88.MirrorCS");Q1=makeQuery(id+"F16.imprint","IMPRINT",FACE,{"disambiguationData":[TD([[makeQuery(id+"F16.imprint","IMPRINT",EDGE,{"derivedFrom":subQ0}),1.0]])]});}
            var Q2;
            Q2=makeQuery(id+"F16.imprint","IMPRINT",FACE,{"disambiguationData":[TD([[makeQuery(id+"F16.imprint","IMPRINT",EDGE,{"derivedFrom":sQuery(id+"F16.wireOp",EDGE,"E79.0")}),-1.0]])]});
            var Q3;
            Q3=makeQuery(id+"F2.opExtrude","CAP_FACE",FACE,{"disambiguationData":[OSD([sQuery(id+"F0.wireOp",EDGE,"E12"),sQuery(id+"F0.wireOp",EDGE,"E13"),sQuery(id+"F0.wireOp",EDGE,"E14"),sQuery(id+"F0.wireOp",EDGE,"E15"),sQuery(id+"F0.wireOp",EDGE,"E17.filletArc"),sQuery(id+"F0.wireOp",EDGE,"E18.filletArc"),sQuery(id+"F0.wireOp",EDGE,"E19.filletArc"),sQuery(id+"F0.wireOp",EDGE,"E20.filletArc"),sQuery(id+"F0.wireOp",EDGE,"E25.0"),sQuery(id+"F0.wireOp",EDGE,"E25.1"),sQuery(id+"F0.wireOp",EDGE,"E25.2"),sQuery(id+"F0.wireOp",EDGE,"E25.3"),sQuery(id+"F0.wireOp",EDGE,"E25.4"),sQuery(id+"F0.wireOp",EDGE,"E25.5"),sQuery(id+"F0.wireOp",EDGE,"E25.6"),sQuery(id+"F0.wireOp",EDGE,"E25.7")])],"isStart":false});
            extrude(context, id + "F17", {"entities" : qUnion([Q0, Q1, Q2]), "endBound" : BoundingType.UP_TO_SURFACE, "depth" : 25 * mm, "endBoundEntityFace" : qUnion([Q3]), "offsetDistance" : 25 * mm});
        }
    });
